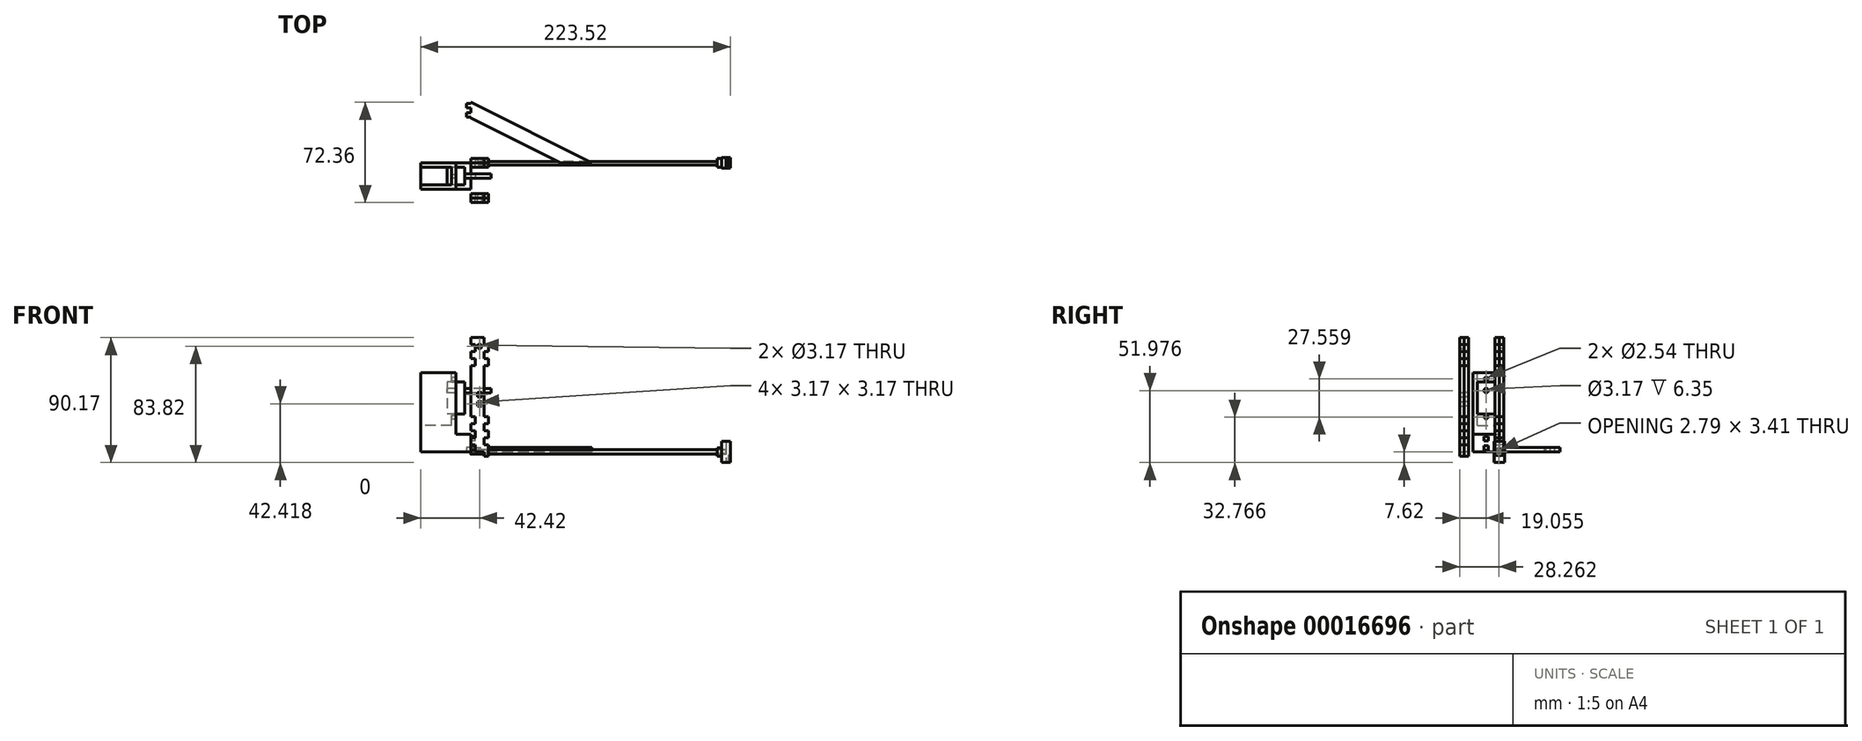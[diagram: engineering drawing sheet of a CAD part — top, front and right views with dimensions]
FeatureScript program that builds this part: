
annotation { "Feature Type Name" : "Feature", "Feature Type Description" : "" }
export const myFeature = defineFeature(function(context is Context, id is Id, definition is map)
    precondition{}
    {
        {
            var Q0;
            Q0=qCreatedBy(makeId("Right.planeOp"),FACE);
            var sketch = newSketch(context, id + "F0", { "sketchPlane" : qUnion([Q0])});
            skCircle(sketch, "E0.0", {"center": v(0, 0) * mm, "radius": 1.59 * mm});
            skPoint(sketch, "E1", {"position": v(0, 1.59) * mm});
            skSolve(sketch);
        }
        {
            var Q0;
            Q0=makeQuery(id+"F0.imprint","IMPRINT",FACE,{"disambiguationData":[TD([[makeQuery(id+"F0.imprint","IMPRINT",EDGE,{"derivedFrom":sQuery(id+"F0.wireOp",EDGE,"E0.0")}),1.0]])]});
            extrude(context, id + "F1", {"entities" : qUnion([Q0]), "depth" : 177.8 * mm});
        }
        {
            var Q0;
            Q0=qCreatedBy(makeId("Top.planeOp"),FACE);
            var Q1;
            Q1=sQuery(id+"F0.wireOp",VERTEX,"E1");
            cPlane(context, id + "F2", {"entities" : qUnion([Q0, Q1]), "cplaneType" : CPlaneType.PLANE_POINT, "offset" : 152.4 * mm, "width" : 152.4 * mm, "height" : 152.4 * mm});
        }
        {
            var Q0;
            Q0=qCreatedBy(id+"F2.planeOp",FACE);
            var sketch = newSketch(context, id + "F3", { "sketchPlane" : qUnion([Q0])});
            skLineSegment(sketch, "E2.0", {"start": v(0, 1.59) * mm, "end": v(0, -1.59) * mm});
            skLineSegment(sketch, "E3", {"start": v(0, 1.59) * mm, "end": v(177.8, 1.59) * mm, "construction": true});
            skLineSegment(sketch, "E4", {"start": v(177.8, -1.59) * mm, "end": v(0, -1.59) * mm, "construction": true});
            skLineSegment(sketch, "E5.bottom", {"start": v(27.11, 1.59) * mm, "end": v(88.9, 1.59) * mm});
            skLineSegment(sketch, "E5.top", {"start": v(27.11, 0.95) * mm, "end": v(88.9, 0.95) * mm});
            skLineSegment(sketch, "E5.left", {"start": v(27.11, 1.59) * mm, "end": v(27.11, 0.95) * mm});
            skLineSegment(sketch, "E5.right", {"start": v(88.9, 1.59) * mm, "end": v(88.9, 0.95) * mm});
            skLineSegment(sketch, "E6.0", {"start": v(177.8, 1.59) * mm, "end": v(177.8, -1.59) * mm});
            skLineSegment(sketch, "E7", {"start": v(88.9, 1.59) * mm, "end": v(88.9, -15.16) * mm, "construction": true});
            skLineSegment(sketch, "E8.0.MirrorCS", {"start": v(150.69, 0.95) * mm, "end": v(88.9, 0.95) * mm});
            skLineSegment(sketch, "E9.0.MirrorCS", {"start": v(150.69, 1.59) * mm, "end": v(88.9, 1.59) * mm});
            skLineSegment(sketch, "E10.0.MirrorCS", {"start": v(150.69, 1.59) * mm, "end": v(150.69, 0.95) * mm});
            skLineSegment(sketch, "E11.bottom", {"start": v(6.35, 1.59) * mm, "end": v(0, 1.59) * mm});
            skLineSegment(sketch, "E11.top", {"start": v(6.35, 0.95) * mm, "end": v(0, 0.95) * mm});
            skLineSegment(sketch, "E11.left", {"start": v(6.35, 1.59) * mm, "end": v(6.35, 0.95) * mm});
            skLineSegment(sketch, "E11.right", {"start": v(0, 1.59) * mm, "end": v(0, 0.95) * mm});
            skLineSegment(sketch, "E12.0.MirrorCS", {"start": v(171.45, 0.95) * mm, "end": v(177.8, 0.95) * mm});
            skLineSegment(sketch, "E13.0.MirrorCS", {"start": v(171.45, 1.59) * mm, "end": v(171.45, 0.95) * mm});
            skLineSegment(sketch, "E14.0.MirrorCS", {"start": v(177.8, 1.59) * mm, "end": v(177.8, 0.95) * mm});
            skLineSegment(sketch, "E15.0.MirrorCS", {"start": v(171.45, 1.59) * mm, "end": v(177.8, 1.59) * mm});
            skLineSegment(sketch, "E16.bottom", {"start": v(27.11, 1.59) * mm, "end": v(6.35, 1.59) * mm});
            skLineSegment(sketch, "E16.top", {"start": v(27.11, 0.95) * mm, "end": v(6.35, 0.95) * mm});
            skLineSegment(sketch, "E17.bottom", {"start": v(150.69, 1.59) * mm, "end": v(171.45, 1.59) * mm});
            skLineSegment(sketch, "E17.top", {"start": v(150.69, 0.95) * mm, "end": v(171.45, 0.95) * mm});
            skSolve(sketch);
        }
        {
            var Q0;
            {Q0=qUnion([makeQuery(id+"F3.imprint","IMPRINT",FACE,{"disambiguationData":[TD([[makeQuery(id+"F3.imprint","IMPRINT",EDGE,{"derivedFrom":sQuery(id+"F3.wireOp",EDGE,"E11.bottom")}),1.0]])]}),makeQuery(id+"F3.imprint","IMPRINT",FACE,{"disambiguationData":[TD([[makeQuery(id+"F3.imprint","IMPRINT",EDGE,{"derivedFrom":sQuery(id+"F3.wireOp",EDGE,"E12.0.MirrorCS")}),1.0]])]}),makeQuery(id+"F3.imprint","IMPRINT",FACE,{"disambiguationData":[TD([[makeQuery(id+"F3.imprint","IMPRINT",EDGE,{"derivedFrom":sQuery(id+"F3.wireOp",EDGE,"E5.bottom")}),-1.0]])]}),makeQuery(id+"F3.imprint","IMPRINT",FACE,{"disambiguationData":[TD([[makeQuery(id+"F3.imprint","IMPRINT",EDGE,{"derivedFrom":sQuery(id+"F3.wireOp",EDGE,"E8.0.MirrorCS")}),-1.0]])]}),makeQuery(id+"F3.imprint","IMPRINT",FACE,{"disambiguationData":[TD([[makeQuery(id+"F3.imprint","IMPRINT",EDGE,{"derivedFrom":sQuery(id+"F3.wireOp",EDGE,"E16.bottom")}),1.0]])]}),makeQuery(id+"F3.imprint","IMPRINT",FACE,{"disambiguationData":[TD([[makeQuery(id+"F3.imprint","IMPRINT",EDGE,{"derivedFrom":sQuery(id+"F3.wireOp",EDGE,"E17.bottom")}),-1.0]])]})]);}
            extrude(context, id + "F4", {"entities" : qUnion([Q0]), "operationType" : NewBodyOperationType.REMOVE, "endBound" : BoundingType.THROUGH_ALL, "oppositeDirection" : true, "depth" : 25.4 * mm});
        }
        {
            var Q0;
            Q0=qCreatedBy(makeId("Front.planeOp"),FACE);
            var sketch = newSketch(context, id + "F5", { "sketchPlane" : qUnion([Q0])});
            skLineSegment(sketch, "E18.bottom", {"start": v(0, 0) * mm, "end": v(12.7, 0) * mm});
            skLineSegment(sketch, "E18.top", {"start": v(0, 82.55) * mm, "end": v(12.7, 82.55) * mm});
            skLineSegment(sketch, "E18.left", {"start": v(0, 0) * mm, "end": v(0, 82.55) * mm});
            skLineSegment(sketch, "E18.right", {"start": v(12.7, 0) * mm, "end": v(12.7, 82.55) * mm});
            skLineSegment(sketch, "E19.bottom", {"start": v(12.7, 0) * mm, "end": v(9.53, 0) * mm});
            skLineSegment(sketch, "E19.top", {"start": v(12.7, -3.17) * mm, "end": v(9.53, -3.17) * mm});
            skLineSegment(sketch, "E19.left", {"start": v(12.7, 0) * mm, "end": v(12.7, -3.17) * mm});
            skLineSegment(sketch, "E19.right", {"start": v(9.53, 0) * mm, "end": v(9.53, -3.17) * mm});
            skLineSegment(sketch, "E20.bottom", {"start": v(12.7, 82.55) * mm, "end": v(9.52, 82.55) * mm});
            skLineSegment(sketch, "E20.top", {"start": v(12.7, 77.47) * mm, "end": v(9.52, 77.47) * mm});
            skLineSegment(sketch, "E20.left", {"start": v(12.7, 82.55) * mm, "end": v(12.7, 77.47) * mm});
            skLineSegment(sketch, "E20.right", {"start": v(9.52, 82.55) * mm, "end": v(9.52, 77.47) * mm});
            skLineSegment(sketch, "E21.bottom", {"start": v(9.52, 72.39) * mm, "end": v(12.7, 72.39) * mm});
            skLineSegment(sketch, "E21.top", {"start": v(9.52, 67.3) * mm, "end": v(12.7, 67.3) * mm});
            skLineSegment(sketch, "E21.left", {"start": v(9.52, 72.39) * mm, "end": v(9.52, 67.3) * mm});
            skLineSegment(sketch, "E21.right", {"start": v(12.7, 72.39) * mm, "end": v(12.7, 67.3) * mm});
            skLineSegment(sketch, "E22.bottom", {"start": v(9.52, 62.23) * mm, "end": v(12.7, 62.23) * mm});
            skLineSegment(sketch, "E22.top", {"start": v(9.53, 25.4) * mm, "end": v(12.7, 25.4) * mm});
            skLineSegment(sketch, "E22.left", {"start": v(9.52, 62.23) * mm, "end": v(9.52, 25.4) * mm});
            skLineSegment(sketch, "E22.right", {"start": v(12.7, 62.23) * mm, "end": v(12.7, 25.4) * mm});
            skLineSegment(sketch, "E23.bottom", {"start": v(9.53, 20.32) * mm, "end": v(12.7, 20.32) * mm});
            skLineSegment(sketch, "E23.top", {"start": v(9.53, 15.24) * mm, "end": v(12.7, 15.24) * mm});
            skLineSegment(sketch, "E23.left", {"start": v(9.52, 20.32) * mm, "end": v(9.52, 15.24) * mm});
            skLineSegment(sketch, "E23.right", {"start": v(12.7, 20.32) * mm, "end": v(12.7, 15.24) * mm});
            skLineSegment(sketch, "E24.bottom", {"start": v(9.53, 10.16) * mm, "end": v(12.7, 10.16) * mm});
            skLineSegment(sketch, "E24.top", {"start": v(9.53, 5.08) * mm, "end": v(12.7, 5.08) * mm});
            skLineSegment(sketch, "E24.left", {"start": v(9.52, 10.16) * mm, "end": v(9.52, 5.08) * mm});
            skLineSegment(sketch, "E24.right", {"start": v(12.7, 10.16) * mm, "end": v(12.7, 5.08) * mm});
            skLineSegment(sketch, "E25.bottom", {"start": v(0, 77.47) * mm, "end": v(3.18, 77.47) * mm});
            skLineSegment(sketch, "E25.top", {"start": v(0, 72.39) * mm, "end": v(3.18, 72.39) * mm});
            skLineSegment(sketch, "E25.left", {"start": v(0, 77.47) * mm, "end": v(0, 72.39) * mm});
            skLineSegment(sketch, "E25.right", {"start": v(3.18, 77.47) * mm, "end": v(3.18, 72.39) * mm});
            skLineSegment(sketch, "E26.bottom", {"start": v(0, 67.3) * mm, "end": v(3.18, 67.3) * mm});
            skLineSegment(sketch, "E26.top", {"start": v(0, 62.23) * mm, "end": v(3.18, 62.23) * mm});
            skLineSegment(sketch, "E26.left", {"start": v(0, 67.3) * mm, "end": v(0, 62.23) * mm});
            skLineSegment(sketch, "E26.right", {"start": v(3.18, 67.3) * mm, "end": v(3.18, 62.23) * mm});
            skLineSegment(sketch, "E27.bottom", {"start": v(0, 25.4) * mm, "end": v(3.18, 25.4) * mm});
            skLineSegment(sketch, "E27.top", {"start": v(0, 20.32) * mm, "end": v(3.18, 20.32) * mm});
            skLineSegment(sketch, "E27.left", {"start": v(0, 25.4) * mm, "end": v(0, 20.32) * mm});
            skLineSegment(sketch, "E27.right", {"start": v(3.18, 25.4) * mm, "end": v(3.18, 20.32) * mm});
            skLineSegment(sketch, "E28.bottom", {"start": v(0, 15.24) * mm, "end": v(3.18, 15.24) * mm});
            skLineSegment(sketch, "E28.top", {"start": v(0, 10.16) * mm, "end": v(3.18, 10.16) * mm});
            skLineSegment(sketch, "E28.left", {"start": v(0, 15.24) * mm, "end": v(0, 10.16) * mm});
            skLineSegment(sketch, "E28.right", {"start": v(3.18, 15.24) * mm, "end": v(3.18, 10.16) * mm});
            skLineSegment(sketch, "E29.bottom", {"start": v(0, 5.08) * mm, "end": v(3.18, 5.08) * mm});
            skLineSegment(sketch, "E29.top", {"start": v(0, 0) * mm, "end": v(3.18, 0) * mm});
            skLineSegment(sketch, "E29.left", {"start": v(0, 5.08) * mm, "end": v(0, 0) * mm});
            skLineSegment(sketch, "E29.right", {"start": v(3.18, 5.08) * mm, "end": v(3.18, 0) * mm});
            skPoint(sketch, "E30", {"position": v(6.35, 82.55) * mm});
            skPoint(sketch, "E31", {"position": v(6.35, 76.2) * mm});
            skSolve(sketch);
        }
        {
            var Q0;
            Q0=makeQuery(id+"F5.imprint","IMPRINT",FACE,{"disambiguationData":[TD([[makeQuery(id+"F5.imprint","IMPRINT",EDGE,{"derivedFrom":sQuery(id+"F5.wireOp",EDGE,"E18.bottom")}),1.0]])]});
            var Q1;
            Q1=makeQuery(id+"F5.imprint","IMPRINT",FACE,{"disambiguationData":[TD([[makeQuery(id+"F5.imprint","IMPRINT",EDGE,{"derivedFrom":sQuery(id+"F5.wireOp",EDGE,"E19.bottom")}),1.0]])]});
            extrude(context, id + "F6", {"entities" : qUnion([Q0, Q1]), "depth" : 3.17 * mm});
        }
        {
            var Q0;
            Q0=qCreatedBy(makeId("Front.planeOp"),FACE);
            var sketch = newSketch(context, id + "F7", { "sketchPlane" : qUnion([Q0])});
            skLineSegment(sketch, "E32.0.0", {"start": v(3.18, 5.08) * mm, "end": v(3.18, 0) * mm});
            skLineSegment(sketch, "E32.0.1", {"start": v(0, 5.08) * mm, "end": v(3.18, 5.08) * mm});
            skLineSegment(sketch, "E32.0.2", {"start": v(0, 5.08) * mm, "end": v(0, 10.16) * mm});
            skLineSegment(sketch, "E32.0.3", {"start": v(0, 10.16) * mm, "end": v(3.18, 10.16) * mm});
            skLineSegment(sketch, "E32.0.4", {"start": v(3.18, 15.24) * mm, "end": v(3.18, 10.16) * mm});
            skLineSegment(sketch, "E32.0.5", {"start": v(0, 15.24) * mm, "end": v(3.18, 15.24) * mm});
            skLineSegment(sketch, "E32.0.6", {"start": v(0, 15.24) * mm, "end": v(0, 20.32) * mm});
            skLineSegment(sketch, "E32.0.7", {"start": v(0, 20.32) * mm, "end": v(3.18, 20.32) * mm});
            skLineSegment(sketch, "E32.0.8", {"start": v(3.18, 25.4) * mm, "end": v(3.18, 20.32) * mm});
            skLineSegment(sketch, "E32.0.9", {"start": v(0, 25.4) * mm, "end": v(3.18, 25.4) * mm});
            skLineSegment(sketch, "E32.0.10", {"start": v(0, 25.4) * mm, "end": v(0, 62.23) * mm});
            skLineSegment(sketch, "E32.0.11", {"start": v(0, 62.23) * mm, "end": v(3.18, 62.23) * mm});
            skLineSegment(sketch, "E32.0.12", {"start": v(3.18, 67.3) * mm, "end": v(3.18, 62.23) * mm});
            skLineSegment(sketch, "E32.0.13", {"start": v(0, 67.3) * mm, "end": v(3.18, 67.3) * mm});
            skLineSegment(sketch, "E32.0.14", {"start": v(0, 67.3) * mm, "end": v(0, 72.39) * mm});
            skLineSegment(sketch, "E32.0.15", {"start": v(0, 72.39) * mm, "end": v(3.18, 72.39) * mm});
            skLineSegment(sketch, "E32.0.16", {"start": v(3.18, 77.47) * mm, "end": v(3.18, 72.39) * mm});
            skLineSegment(sketch, "E32.0.17", {"start": v(0, 77.47) * mm, "end": v(3.18, 77.47) * mm});
            skLineSegment(sketch, "E32.0.18", {"start": v(0, 77.47) * mm, "end": v(0, 82.55) * mm});
            skLineSegment(sketch, "E32.0.19", {"start": v(0, 82.55) * mm, "end": v(9.52, 82.55) * mm});
            skLineSegment(sketch, "E32.0.20", {"start": v(9.52, 82.55) * mm, "end": v(9.52, 77.47) * mm});
            skLineSegment(sketch, "E32.0.21", {"start": v(12.7, 77.47) * mm, "end": v(9.52, 77.47) * mm});
            skLineSegment(sketch, "E32.0.22", {"start": v(12.7, 72.39) * mm, "end": v(12.7, 77.47) * mm});
            skLineSegment(sketch, "E32.0.23", {"start": v(9.52, 72.39) * mm, "end": v(12.7, 72.39) * mm});
            skLineSegment(sketch, "E32.0.24", {"start": v(9.52, 72.39) * mm, "end": v(9.52, 67.3) * mm});
            skLineSegment(sketch, "E32.0.25", {"start": v(9.52, 67.3) * mm, "end": v(12.7, 67.3) * mm});
            skLineSegment(sketch, "E32.0.26", {"start": v(12.7, 62.23) * mm, "end": v(12.7, 67.3) * mm});
            skLineSegment(sketch, "E32.0.27", {"start": v(9.52, 62.23) * mm, "end": v(12.7, 62.23) * mm});
            skLineSegment(sketch, "E32.0.28", {"start": v(9.52, 62.23) * mm, "end": v(9.52, 25.4) * mm});
            skLineSegment(sketch, "E32.0.29", {"start": v(9.52, 25.4) * mm, "end": v(12.7, 25.4) * mm});
            skLineSegment(sketch, "E32.0.30", {"start": v(12.7, 20.32) * mm, "end": v(12.7, 25.4) * mm});
            skLineSegment(sketch, "E32.0.31", {"start": v(9.53, 20.32) * mm, "end": v(12.7, 20.32) * mm});
            skLineSegment(sketch, "E32.0.32", {"start": v(9.52, 20.32) * mm, "end": v(9.52, 15.24) * mm});
            skLineSegment(sketch, "E32.0.33", {"start": v(9.52, 15.24) * mm, "end": v(12.7, 15.24) * mm});
            skLineSegment(sketch, "E32.0.34", {"start": v(12.7, 10.16) * mm, "end": v(12.7, 15.24) * mm});
            skLineSegment(sketch, "E32.0.35", {"start": v(9.53, 10.16) * mm, "end": v(12.7, 10.16) * mm});
            skLineSegment(sketch, "E32.0.36", {"start": v(9.52, 10.16) * mm, "end": v(9.52, 5.08) * mm});
            skLineSegment(sketch, "E32.0.37", {"start": v(9.52, 5.08) * mm, "end": v(12.7, 5.08) * mm});
            skLineSegment(sketch, "E32.0.38", {"start": v(12.7, -3.17) * mm, "end": v(12.7, 5.08) * mm});
            skLineSegment(sketch, "E32.0.39", {"start": v(12.7, -3.17) * mm, "end": v(9.53, -3.17) * mm});
            skLineSegment(sketch, "E32.0.40", {"start": v(9.53, 0) * mm, "end": v(9.53, -3.17) * mm});
            skLineSegment(sketch, "E32.0.41", {"start": v(3.18, 0) * mm, "end": v(9.53, 0) * mm});
            skLineSegment(sketch, "E33", {"start": v(6.35, 82.55) * mm, "end": v(6.35, 0) * mm, "construction": true});
            skCircle(sketch, "E34", {"center": v(6.35, 76.2) * mm, "radius": 1.59 * mm});
            skSolve(sketch);
        }
        {
            var Q0;
            Q0=makeQuery(id+"F7.imprint","IMPRINT",FACE,{"disambiguationData":[TD([[makeQuery(id+"F7.imprint","IMPRINT",EDGE,{"derivedFrom":sQuery(id+"F7.wireOp",EDGE,"E32.0.0")}),1.0]])]});
            extrude(context, id + "F8", {"entities" : qUnion([Q0]), "oppositeDirection" : true, "depth" : 3.17 * mm});
        }
        {
            var Q0;
            Q0=qCreatedBy(makeId("Front.planeOp"),FACE);
            cPlane(context, id + "F9", {"entities" : qUnion([Q0]), "cplaneType" : CPlaneType.OFFSET, "offset" : 25.4 * mm, "width" : 152.4 * mm, "height" : 152.4 * mm});
        }
        {
            var Q0;
            Q0=qCreatedBy(id+"F9.planeOp",FACE);
            var sketch = newSketch(context, id + "F10", { "sketchPlane" : qUnion([Q0])});
            skLineSegment(sketch, "E35.0.0", {"start": v(0, 5.08) * mm, "end": v(3.18, 5.08) * mm});
            skLineSegment(sketch, "E35.0.1", {"start": v(0, 5.08) * mm, "end": v(0, 10.16) * mm});
            skLineSegment(sketch, "E35.0.2", {"start": v(0, 10.16) * mm, "end": v(3.18, 10.16) * mm});
            skLineSegment(sketch, "E35.0.3", {"start": v(3.18, 15.24) * mm, "end": v(3.18, 10.16) * mm});
            skLineSegment(sketch, "E35.0.4", {"start": v(0, 15.24) * mm, "end": v(3.18, 15.24) * mm});
            skLineSegment(sketch, "E35.0.5", {"start": v(0, 15.24) * mm, "end": v(0, 20.32) * mm});
            skLineSegment(sketch, "E35.0.6", {"start": v(0, 20.32) * mm, "end": v(3.18, 20.32) * mm});
            skLineSegment(sketch, "E35.0.7", {"start": v(3.18, 25.4) * mm, "end": v(3.18, 20.32) * mm});
            skLineSegment(sketch, "E35.0.8", {"start": v(0, 25.4) * mm, "end": v(3.18, 25.4) * mm});
            skLineSegment(sketch, "E35.0.9", {"start": v(0, 25.4) * mm, "end": v(0, 62.23) * mm});
            skLineSegment(sketch, "E35.0.10", {"start": v(0, 62.23) * mm, "end": v(3.18, 62.23) * mm});
            skLineSegment(sketch, "E35.0.11", {"start": v(3.18, 67.3) * mm, "end": v(3.18, 62.23) * mm});
            skLineSegment(sketch, "E35.0.12", {"start": v(0, 67.3) * mm, "end": v(3.18, 67.3) * mm});
            skLineSegment(sketch, "E35.0.13", {"start": v(0, 67.3) * mm, "end": v(0, 72.39) * mm});
            skLineSegment(sketch, "E35.0.14", {"start": v(0, 72.39) * mm, "end": v(3.18, 72.39) * mm});
            skLineSegment(sketch, "E35.0.15", {"start": v(3.18, 77.47) * mm, "end": v(3.18, 72.39) * mm});
            skLineSegment(sketch, "E35.0.16", {"start": v(0, 77.47) * mm, "end": v(3.18, 77.47) * mm});
            skLineSegment(sketch, "E35.0.17", {"start": v(0, 77.47) * mm, "end": v(0, 82.55) * mm});
            skLineSegment(sketch, "E35.0.18", {"start": v(0, 82.55) * mm, "end": v(9.52, 82.55) * mm});
            skLineSegment(sketch, "E35.0.19", {"start": v(9.52, 82.55) * mm, "end": v(9.52, 77.47) * mm});
            skLineSegment(sketch, "E35.0.20", {"start": v(12.7, 77.47) * mm, "end": v(9.52, 77.47) * mm});
            skLineSegment(sketch, "E35.0.21", {"start": v(12.7, 72.39) * mm, "end": v(12.7, 77.47) * mm});
            skLineSegment(sketch, "E35.0.22", {"start": v(9.52, 72.39) * mm, "end": v(12.7, 72.39) * mm});
            skLineSegment(sketch, "E35.0.23", {"start": v(9.52, 72.39) * mm, "end": v(9.52, 67.3) * mm});
            skLineSegment(sketch, "E35.0.24", {"start": v(9.52, 67.3) * mm, "end": v(12.7, 67.3) * mm});
            skLineSegment(sketch, "E35.0.25", {"start": v(12.7, 62.23) * mm, "end": v(12.7, 67.3) * mm});
            skLineSegment(sketch, "E35.0.26", {"start": v(9.52, 62.23) * mm, "end": v(12.7, 62.23) * mm});
            skLineSegment(sketch, "E35.0.27", {"start": v(9.52, 62.23) * mm, "end": v(9.52, 25.4) * mm});
            skLineSegment(sketch, "E35.0.28", {"start": v(9.52, 25.4) * mm, "end": v(12.7, 25.4) * mm});
            skLineSegment(sketch, "E35.0.29", {"start": v(12.7, 20.32) * mm, "end": v(12.7, 25.4) * mm});
            skLineSegment(sketch, "E35.0.30", {"start": v(9.53, 20.32) * mm, "end": v(12.7, 20.32) * mm});
            skLineSegment(sketch, "E35.0.31", {"start": v(9.52, 20.32) * mm, "end": v(9.52, 15.24) * mm});
            skLineSegment(sketch, "E35.0.32", {"start": v(9.52, 15.24) * mm, "end": v(12.7, 15.24) * mm});
            skLineSegment(sketch, "E35.0.33", {"start": v(12.7, 10.16) * mm, "end": v(12.7, 15.24) * mm});
            skLineSegment(sketch, "E35.0.34", {"start": v(9.53, 10.16) * mm, "end": v(12.7, 10.16) * mm});
            skLineSegment(sketch, "E35.0.35", {"start": v(9.52, 10.16) * mm, "end": v(9.52, 5.08) * mm});
            skLineSegment(sketch, "E35.0.36", {"start": v(9.52, 5.08) * mm, "end": v(12.7, 5.08) * mm});
            skLineSegment(sketch, "E35.0.37", {"start": v(12.7, -3.17) * mm, "end": v(12.7, 5.08) * mm});
            skLineSegment(sketch, "E35.0.38", {"start": v(12.7, -3.17) * mm, "end": v(9.53, -3.17) * mm});
            skLineSegment(sketch, "E35.0.39", {"start": v(9.53, 0) * mm, "end": v(9.53, -3.17) * mm});
            skLineSegment(sketch, "E35.0.40", {"start": v(3.18, 0) * mm, "end": v(9.53, 0) * mm});
            skLineSegment(sketch, "E35.0.41", {"start": v(3.18, 5.08) * mm, "end": v(3.18, 0) * mm});
            skLineSegment(sketch, "E36.0", {"start": v(6.35, 82.55) * mm, "end": v(6.35, 0) * mm, "construction": true});
            skLineSegment(sketch, "E37.rect.bottom", {"start": v(4.76, 39.81) * mm, "end": v(7.94, 39.81) * mm});
            skLineSegment(sketch, "E37.rect.top", {"start": v(4.76, 42.99) * mm, "end": v(7.94, 42.99) * mm});
            skLineSegment(sketch, "E37.rect.left", {"start": v(4.76, 39.81) * mm, "end": v(4.76, 42.99) * mm});
            skLineSegment(sketch, "E37.rect.right", {"start": v(7.94, 39.81) * mm, "end": v(7.94, 42.99) * mm});
            skPoint(sketch, "E37.rect.middle", {"position": v(6.35, 41.4) * mm});
            skLineSegment(sketch, "E38.rect.bottom", {"start": v(4.76, 33.21) * mm, "end": v(7.94, 33.21) * mm});
            skLineSegment(sketch, "E38.rect.top", {"start": v(4.76, 36.39) * mm, "end": v(7.94, 36.39) * mm});
            skLineSegment(sketch, "E38.rect.left", {"start": v(4.76, 33.21) * mm, "end": v(4.76, 36.39) * mm});
            skLineSegment(sketch, "E38.rect.right", {"start": v(7.94, 33.21) * mm, "end": v(7.94, 36.39) * mm});
            skPoint(sketch, "E38.rect.middle", {"position": v(6.35, 34.8) * mm});
            skPoint(sketch, "E39", {"position": v(6.35, 38.1) * mm});
            skCircle(sketch, "E40.0", {"center": v(6.35, 76.2) * mm, "radius": 1.59 * mm});
            skSolve(sketch);
        }
        {
            var Q0;
            Q0=makeQuery(id+"F10.imprint","IMPRINT",FACE,{"disambiguationData":[TD([[makeQuery(id+"F10.imprint","IMPRINT",EDGE,{"derivedFrom":sQuery(id+"F10.wireOp",EDGE,"E35.0.0")}),1.0]])]});
            extrude(context, id + "F11", {"entities" : qUnion([Q0]), "depth" : 3.17 * mm});
        }
        {
            var Q0;
            Q0=qCreatedBy(id+"F9.planeOp",FACE);
            var sketch = newSketch(context, id + "F12", { "sketchPlane" : qUnion([Q0])});
            skLineSegment(sketch, "E41.0.0", {"start": v(0, 5.08) * mm, "end": v(0, 10.16) * mm});
            skLineSegment(sketch, "E41.0.1", {"start": v(0, 10.16) * mm, "end": v(3.18, 10.16) * mm});
            skLineSegment(sketch, "E41.0.2", {"start": v(3.18, 15.24) * mm, "end": v(3.18, 10.16) * mm});
            skLineSegment(sketch, "E41.0.3", {"start": v(0, 15.24) * mm, "end": v(3.18, 15.24) * mm});
            skLineSegment(sketch, "E41.0.4", {"start": v(0, 15.24) * mm, "end": v(0, 20.32) * mm});
            skLineSegment(sketch, "E41.0.5", {"start": v(0, 20.32) * mm, "end": v(3.18, 20.32) * mm});
            skLineSegment(sketch, "E41.0.6", {"start": v(3.18, 25.4) * mm, "end": v(3.18, 20.32) * mm});
            skLineSegment(sketch, "E41.0.7", {"start": v(0, 25.4) * mm, "end": v(3.18, 25.4) * mm});
            skLineSegment(sketch, "E41.0.8", {"start": v(0, 25.4) * mm, "end": v(0, 62.23) * mm});
            skLineSegment(sketch, "E41.0.9", {"start": v(0, 62.23) * mm, "end": v(3.18, 62.23) * mm});
            skLineSegment(sketch, "E41.0.10", {"start": v(3.18, 67.3) * mm, "end": v(3.18, 62.23) * mm});
            skLineSegment(sketch, "E41.0.11", {"start": v(0, 67.3) * mm, "end": v(3.18, 67.3) * mm});
            skLineSegment(sketch, "E41.0.12", {"start": v(0, 67.3) * mm, "end": v(0, 72.39) * mm});
            skLineSegment(sketch, "E41.0.13", {"start": v(0, 72.39) * mm, "end": v(3.18, 72.39) * mm});
            skLineSegment(sketch, "E41.0.14", {"start": v(3.18, 77.47) * mm, "end": v(3.18, 72.39) * mm});
            skLineSegment(sketch, "E41.0.15", {"start": v(0, 77.47) * mm, "end": v(3.18, 77.47) * mm});
            skLineSegment(sketch, "E41.0.16", {"start": v(0, 77.47) * mm, "end": v(0, 82.55) * mm});
            skLineSegment(sketch, "E41.0.17", {"start": v(0, 82.55) * mm, "end": v(9.52, 82.55) * mm});
            skLineSegment(sketch, "E41.0.18", {"start": v(9.52, 82.55) * mm, "end": v(9.52, 77.47) * mm});
            skLineSegment(sketch, "E41.0.19", {"start": v(12.7, 77.47) * mm, "end": v(9.52, 77.47) * mm});
            skLineSegment(sketch, "E41.0.20", {"start": v(12.7, 72.39) * mm, "end": v(12.7, 77.47) * mm});
            skLineSegment(sketch, "E41.0.21", {"start": v(9.52, 72.39) * mm, "end": v(12.7, 72.39) * mm});
            skLineSegment(sketch, "E41.0.22", {"start": v(9.52, 72.39) * mm, "end": v(9.52, 67.3) * mm});
            skLineSegment(sketch, "E41.0.23", {"start": v(9.52, 67.3) * mm, "end": v(12.7, 67.3) * mm});
            skLineSegment(sketch, "E41.0.24", {"start": v(12.7, 62.23) * mm, "end": v(12.7, 67.3) * mm});
            skLineSegment(sketch, "E41.0.25", {"start": v(9.52, 62.23) * mm, "end": v(12.7, 62.23) * mm});
            skLineSegment(sketch, "E41.0.26", {"start": v(9.52, 62.23) * mm, "end": v(9.52, 25.4) * mm});
            skLineSegment(sketch, "E41.0.27", {"start": v(9.52, 25.4) * mm, "end": v(12.7, 25.4) * mm});
            skLineSegment(sketch, "E41.0.28", {"start": v(12.7, 20.32) * mm, "end": v(12.7, 25.4) * mm});
            skLineSegment(sketch, "E41.0.29", {"start": v(9.53, 20.32) * mm, "end": v(12.7, 20.32) * mm});
            skLineSegment(sketch, "E41.0.30", {"start": v(9.52, 20.32) * mm, "end": v(9.52, 15.24) * mm});
            skLineSegment(sketch, "E41.0.31", {"start": v(9.52, 15.24) * mm, "end": v(12.7, 15.24) * mm});
            skLineSegment(sketch, "E41.0.32", {"start": v(12.7, 10.16) * mm, "end": v(12.7, 15.24) * mm});
            skLineSegment(sketch, "E41.0.33", {"start": v(9.53, 10.16) * mm, "end": v(12.7, 10.16) * mm});
            skLineSegment(sketch, "E41.0.34", {"start": v(9.52, 10.16) * mm, "end": v(9.52, 5.08) * mm});
            skLineSegment(sketch, "E41.0.35", {"start": v(9.52, 5.08) * mm, "end": v(12.7, 5.08) * mm});
            skLineSegment(sketch, "E41.0.36", {"start": v(12.7, -3.17) * mm, "end": v(12.7, 5.08) * mm});
            skLineSegment(sketch, "E41.0.37", {"start": v(12.7, -3.17) * mm, "end": v(9.53, -3.17) * mm});
            skLineSegment(sketch, "E41.0.38", {"start": v(9.53, 0) * mm, "end": v(9.53, -3.17) * mm});
            skLineSegment(sketch, "E41.0.39", {"start": v(3.18, 0) * mm, "end": v(9.53, 0) * mm});
            skLineSegment(sketch, "E41.0.40", {"start": v(3.18, 5.08) * mm, "end": v(3.18, 0) * mm});
            skLineSegment(sketch, "E41.0.41", {"start": v(0, 5.08) * mm, "end": v(3.18, 5.08) * mm});
            skLineSegment(sketch, "E42.0", {"start": v(4.76, 39.81) * mm, "end": v(7.94, 39.81) * mm});
            skLineSegment(sketch, "E43.0", {"start": v(7.94, 39.81) * mm, "end": v(7.94, 42.99) * mm});
            skLineSegment(sketch, "E44.0", {"start": v(4.76, 42.99) * mm, "end": v(7.94, 42.99) * mm});
            skLineSegment(sketch, "E45.0", {"start": v(4.76, 39.81) * mm, "end": v(4.76, 42.99) * mm});
            skLineSegment(sketch, "E46.0", {"start": v(4.76, 36.39) * mm, "end": v(7.94, 36.39) * mm});
            skLineSegment(sketch, "E47.0", {"start": v(7.94, 33.21) * mm, "end": v(7.94, 36.39) * mm});
            skLineSegment(sketch, "E48.0", {"start": v(4.76, 33.21) * mm, "end": v(7.94, 33.21) * mm});
            skLineSegment(sketch, "E49.0", {"start": v(4.76, 33.21) * mm, "end": v(4.76, 36.39) * mm});
            skSolve(sketch);
        }
        {
            var Q0;
            Q0=makeQuery(id+"F12.imprint","IMPRINT",FACE,{"disambiguationData":[TD([[makeQuery(id+"F12.imprint","IMPRINT",EDGE,{"derivedFrom":sQuery(id+"F12.wireOp",EDGE,"E41.0.0")}),-1.0]])]});
            extrude(context, id + "F13", {"entities" : qUnion([Q0]), "oppositeDirection" : true, "depth" : 3.17 * mm});
        }
        {
            var Q0;
            Q0=qCreatedBy(makeId("Top.planeOp"),FACE);
            var sketch = newSketch(context, id + "F14", { "sketchPlane" : qUnion([Q0])});
            skPoint(sketch, "E50", {"position": v(76.2, 0) * mm});
            skPoint(sketch, "E51", {"position": v(0, 38.1) * mm});
            skLineSegment(sketch, "E52", {"start": v(0, 32.42) * mm, "end": v(64.84, 0) * mm});
            skLineSegment(sketch, "E53", {"start": v(87.56, 0) * mm, "end": v(0, 43.78) * mm});
            skLineSegment(sketch, "E54", {"start": v(0, 43.78) * mm, "end": v(0, 32.42) * mm});
            skPoint(sketch, "E55.orphan", {"position": v(2.27, 42.64) * mm});
            skPoint(sketch, "E56.orphan", {"position": v(-2.27, 33.56) * mm});
            skLineSegment(sketch, "E57", {"start": v(64.84, 0) * mm, "end": v(87.56, 0) * mm});
            skPoint(sketch, "E58.orphan", {"position": v(73.93, -4.54) * mm});
            skPoint(sketch, "E59.end.orphan", {"position": v(78.47, 4.54) * mm});
            skLineSegment(sketch, "E60.bottom", {"start": v(0, 39.81) * mm, "end": v(-3.17, 39.81) * mm});
            skLineSegment(sketch, "E60.top", {"start": v(0, 42.99) * mm, "end": v(-3.17, 42.99) * mm});
            skLineSegment(sketch, "E60.right", {"start": v(-3.17, 39.81) * mm, "end": v(-3.17, 42.99) * mm});
            skLineSegment(sketch, "E61.bottom", {"start": v(0, 33.21) * mm, "end": v(-3.17, 33.21) * mm});
            skLineSegment(sketch, "E61.top", {"start": v(0, 36.39) * mm, "end": v(-3.17, 36.39) * mm});
            skLineSegment(sketch, "E61.right", {"start": v(-3.17, 33.21) * mm, "end": v(-3.17, 36.39) * mm});
            skLineSegment(sketch, "E62.bottom", {"start": v(77.91, 0) * mm, "end": v(81.09, 0) * mm});
            skLineSegment(sketch, "E62.top", {"start": v(77.91, -3.17) * mm, "end": v(81.09, -3.17) * mm});
            skLineSegment(sketch, "E62.left", {"start": v(77.91, 0) * mm, "end": v(77.91, -3.17) * mm});
            skLineSegment(sketch, "E62.right", {"start": v(81.09, 0) * mm, "end": v(81.09, -3.17) * mm});
            skLineSegment(sketch, "E63.bottom", {"start": v(71.31, 0) * mm, "end": v(74.49, 0) * mm});
            skLineSegment(sketch, "E63.top", {"start": v(71.31, -3.17) * mm, "end": v(74.49, -3.17) * mm});
            skLineSegment(sketch, "E63.left", {"start": v(71.31, 0) * mm, "end": v(71.31, -3.17) * mm});
            skLineSegment(sketch, "E63.right", {"start": v(74.49, 0) * mm, "end": v(74.49, -3.17) * mm});
            skSolve(sketch);
        }
        {
            var Q0;
            {var subQ1=sQuery(id+"F14.wireOp",EDGE,"E60.bottom");var subQ7=sQuery(id+"F14.wireOp",EDGE,"E61.bottom");var subQ13=sQuery(id+"F14.wireOp",EDGE,"E62.bottom");var subQ14=makeQuery(id+"F14.imprint","IMPRINT",EDGE,{"derivedFrom":subQ13});var subQ17=sQuery(id+"F14.wireOp",EDGE,"E63.bottom");var subQ18=makeQuery(id+"F14.imprint","IMPRINT",EDGE,{"derivedFrom":subQ17});var subQ21=sQuery(id+"F14.wireOp",EDGE,"E52");Q0=qUnion([makeQuery(id+"F14.imprint","IMPRINT",FACE,{"disambiguationData":[TD([[makeQuery(id+"F14.imprint","IMPRINT",EDGE,{"derivedFrom":subQ1}),-1.0]])]}),makeQuery(id+"F14.imprint","IMPRINT",FACE,{"disambiguationData":[TD([[makeQuery(id+"F14.imprint","IMPRINT",EDGE,{"derivedFrom":subQ7}),-1.0]])]}),makeQuery(id+"F14.imprint","IMPRINT",FACE,{"disambiguationData":[TD([[subQ14,-1.0]])]}),makeQuery(id+"F14.imprint","IMPRINT",FACE,{"disambiguationData":[TD([[subQ18,-1.0]])]}),makeQuery(id+"F14.imprint","IMPRINT",FACE,{"disambiguationData":[TD([[makeQuery(id+"F14.imprint","IMPRINT",EDGE,{"derivedFrom":subQ21}),1.0]])]})]);}
            extrude(context, id + "F15", {"entities" : qUnion([Q0]), "depth" : 3.17 * mm});
        }
        {
            var Q0;
            Q0=makeQuery(id+"F1.opExtrude","CAP_FACE",FACE,{"disambiguationData":[OSD([sQuery(id+"F0.wireOp",EDGE,"E0.0")])],"isStart":false});
            var sketch = newSketch(context, id + "F16", { "sketchPlane" : qUnion([Q0])});
            skLineSegment(sketch, "E64.0.0", {"start": v(0.95, -1.27) * mm, "end": v(0.95, 1.27) * mm});
            skArc(sketch, "E64.0.1", {"start": v(0.95, 1.27) * mm, "mid": v(-1.59, 0) * mm, "end": v(0.95, -1.27) * mm});
            skCircle(sketch, "E65", {"center": v(0, 0) * mm, "radius": 3.08 * mm});
            skLineSegment(sketch, "E66.0", {"start": v(1.08, -1.33) * mm, "end": v(1.08, 1.33) * mm});
            skArc(sketch, "E66.1", {"start": v(1.08, 1.33) * mm, "mid": v(-1.71, 0) * mm, "end": v(1.08, -1.33) * mm});
            skSolve(sketch);
        }
        {
            var Q0;
            Q0=makeQuery(id+"F16.imprint","IMPRINT",FACE,{"disambiguationData":[TD([[makeQuery(id+"F16.imprint","IMPRINT",EDGE,{"derivedFrom":sQuery(id+"F16.wireOp",EDGE,"E65")}),1.0]])]});
            extrude(context, id + "F17", {"entities" : qUnion([Q0]), "depth" : 6.35 * mm});
        }
        {
            var Q0;
            Q0=makeQuery(id+"F17.opExtrude","CAP_FACE",FACE,{"disambiguationData":[OSD([sQuery(id+"F16.wireOp",EDGE,"E65"),sQuery(id+"F16.wireOp",EDGE,"E66.0"),sQuery(id+"F16.wireOp",EDGE,"E66.1")])],"isStart":false});
            var sketch = newSketch(context, id + "F18", { "sketchPlane" : qUnion([Q0])});
            skLineSegment(sketch, "E67.rect.bottom", {"start": v(3.8, -7.62) * mm, "end": v(-3.81, -7.62) * mm});
            skLineSegment(sketch, "E67.rect.top", {"start": v(3.8, 7.62) * mm, "end": v(-3.81, 7.62) * mm});
            skLineSegment(sketch, "E67.rect.left", {"start": v(3.81, -7.62) * mm, "end": v(3.81, 7.62) * mm});
            skLineSegment(sketch, "E67.rect.right", {"start": v(-3.81, -7.62) * mm, "end": v(-3.8, 7.62) * mm});
            skPoint(sketch, "E67.rect.middle", {"position": v(0, 0) * mm});
            skSolve(sketch);
        }
        {
            var Q0;
            Q0=makeQuery(id+"F18.imprint","IMPRINT",FACE,{"disambiguationData":[TD([[makeQuery(id+"F18.imprint","IMPRINT",EDGE,{"derivedFrom":sQuery(id+"F18.wireOp",EDGE,"E67.rect.bottom")}),-1.0]])]});
            var Q1;
            Q1=makeQuery(id+"F18.imprint","IMPRINT",FACE,{"disambiguationData":[TD([[makeQuery(id+"F18.imprint","IMPRINT",EDGE,{"derivedFrom":makeQuery(id+"F17.opExtrude","CAP_EDGE",EDGE,{"disambiguationData":[OSD([sQuery(id+"F16.wireOp",EDGE,"E65")])],"isStart":false})}),1.0]])]});
            extrude(context, id + "F19", {"entities" : qUnion([Q0, Q1]), "operationType" : NewBodyOperationType.ADD, "oppositeDirection" : true, "depth" : 3.17 * mm});
        }
        {
            var Q0;
            {var subQ0=sQuery(id+"F16.wireOp",EDGE,"E66.0");var subQ1=sQuery(id+"F16.wireOp",EDGE,"E66.1");Q0=makeQuery(id+"F19.boolean.opBoolean","MERGE",FACE,{"derivedFrom":[makeQuery(id+"F17.opExtrude","CAP_FACE",FACE,{"disambiguationData":[OSD([sQuery(id+"F16.wireOp",EDGE,"E65"),subQ0,subQ1])],"isStart":false}),makeQuery(id+"F19.opExtrude","CAP_FACE",FACE,{"disambiguationData":[OSD([subQ0,subQ1,sQuery(id+"F18.wireOp",EDGE,"E67.rect.bottom"),sQuery(id+"F18.wireOp",EDGE,"E67.rect.top"),sQuery(id+"F18.wireOp",EDGE,"E67.rect.left"),sQuery(id+"F18.wireOp",EDGE,"E67.rect.right")])],"isStart":true})]});}
            var sketch = newSketch(context, id + "F20", { "sketchPlane" : qUnion([Q0])});
            skLineSegment(sketch, "E68.bottom", {"start": v(-3.09, 7.62) * mm, "end": v(3.09, 7.62) * mm});
            skLineSegment(sketch, "E68.top", {"start": v(-3.09, -7.62) * mm, "end": v(3.09, -7.62) * mm});
            skLineSegment(sketch, "E68.left", {"start": v(-3.09, 7.62) * mm, "end": v(-3.09, -7.62) * mm});
            skLineSegment(sketch, "E68.right", {"start": v(3.09, 7.62) * mm, "end": v(3.09, -7.62) * mm});
            skPoint(sketch, "E69", {"position": v(0, 7.62) * mm});
            skLineSegment(sketch, "E70", {"start": v(-3.09, -2.54) * mm, "end": v(3.09, -2.54) * mm});
            skSolve(sketch);
        }
        {
            var Q0;
            {var subQ3=makeQuery(id+"F19.opExtrude","CAP_EDGE",EDGE,{"disambiguationData":[OSD([sQuery(id+"F18.wireOp",EDGE,"E67.rect.right")])],"isStart":true});Q0=makeQuery(id+"F20.imprint","IMPRINT",FACE,{"disambiguationData":[TD([[makeQuery(id+"F20.imprint","IMPRINT",EDGE,{"derivedFrom":subQ3}),-1.0]])]});}
            var Q1;
            {var subQ3=sQuery(id+"F20.wireOp",EDGE,"E68.top");Q1=makeQuery(id+"F20.imprint","IMPRINT",FACE,{"disambiguationData":[TD([[makeQuery(id+"F20.imprint","IMPRINT",EDGE,{"derivedFrom":subQ3}),-1.0]])]});}
            var Q2;
            {var subQ3=makeQuery(id+"F19.opExtrude","CAP_EDGE",EDGE,{"disambiguationData":[OSD([sQuery(id+"F18.wireOp",EDGE,"E67.rect.left")])],"isStart":true});Q2=makeQuery(id+"F20.imprint","IMPRINT",FACE,{"disambiguationData":[TD([[makeQuery(id+"F20.imprint","IMPRINT",EDGE,{"derivedFrom":subQ3}),1.0]])]});}
            extrude(context, id + "F21", {"entities" : qUnion([Q0, Q1, Q2]), "operationType" : NewBodyOperationType.ADD, "depth" : 3.3 * mm});
        }
        {
            var Q0;
            {var subQ3=sQuery(id+"F20.wireOp",EDGE,"E68.top");Q0=makeQuery(id+"F20.imprint","IMPRINT",FACE,{"disambiguationData":[TD([[makeQuery(id+"F20.imprint","IMPRINT",EDGE,{"derivedFrom":subQ3}),-1.0]])]});}
            extrude(context, id + "F22", {"entities" : qUnion([Q0]), "operationType" : NewBodyOperationType.REMOVE, "depth" : 1.65 * mm});
        }
        {
            var Q0;
            Q0=qCreatedBy(makeId("Front.planeOp"),FACE);
            var sketch = newSketch(context, id + "F23", { "sketchPlane" : qUnion([Q0])});
            skLineSegment(sketch, "E71.bottom", {"start": v(0, 0) * mm, "end": v(-36.07, 0) * mm});
            skLineSegment(sketch, "E71.top", {"start": v(-10.67, 57.15) * mm, "end": v(-36.07, 57.15) * mm});
            skLineSegment(sketch, "E71.left", {"start": v(0, 0) * mm, "end": v(0, 12.7) * mm});
            skLineSegment(sketch, "E71.right", {"start": v(-36.07, 0) * mm, "end": v(-36.07, 57.15) * mm});
            skLineSegment(sketch, "E72.top", {"start": v(-10.67, 12.7) * mm, "end": v(0, 12.7) * mm});
            skLineSegment(sketch, "E72.left", {"start": v(-10.67, 57.15) * mm, "end": v(-10.67, 12.7) * mm});
            skPoint(sketch, "E73", {"position": v(0, 6.35) * mm});
            skPoint(sketch, "E74", {"position": v(-10.67, 44.45) * mm});
            skSolve(sketch);
        }
        {
            var Q0;
            Q0=makeQuery(id+"F23.imprint","IMPRINT",FACE,{"disambiguationData":[TD([[makeQuery(id+"F23.imprint","IMPRINT",EDGE,{"derivedFrom":sQuery(id+"F23.wireOp",EDGE,"E71.bottom")}),-1.0]])]});
            extrude(context, id + "F24", {"entities" : qUnion([Q0]), "depth" : 19.05 * mm});
        }
        {
            var Q0;
            Q0=makeQuery(id+"F24.opExtrude","SWEPT_FACE",FACE,{"disambiguationData":[OSD([sQuery(id+"F23.wireOp",EDGE,"E71.left")])]});
            var sketch = newSketch(context, id + "F25", { "sketchPlane" : qUnion([Q0])});
            skLineSegment(sketch, "E75", {"start": v(-9.53, 12.7) * mm, "end": v(-9.53, 0) * mm, "construction": true});
            skLineSegment(sketch, "E76", {"start": v(-19.05, 6.35) * mm, "end": v(0, 6.35) * mm, "construction": true});
            skLineSegment(sketch, "E77.rect.bottom", {"start": v(-7.94, 8.06) * mm, "end": v(-11.11, 8.06) * mm});
            skLineSegment(sketch, "E77.rect.top", {"start": v(-7.94, 11.24) * mm, "end": v(-11.11, 11.24) * mm});
            skLineSegment(sketch, "E77.rect.left", {"start": v(-7.94, 8.06) * mm, "end": v(-7.94, 11.24) * mm});
            skLineSegment(sketch, "E77.rect.right", {"start": v(-11.11, 8.06) * mm, "end": v(-11.11, 11.24) * mm});
            skPoint(sketch, "E77.rect.middle", {"position": v(-9.53, 9.65) * mm});
            skLineSegment(sketch, "E78.rect.bottom", {"start": v(-7.94, 1.46) * mm, "end": v(-11.11, 1.46) * mm});
            skLineSegment(sketch, "E78.rect.top", {"start": v(-7.94, 4.64) * mm, "end": v(-11.11, 4.64) * mm});
            skLineSegment(sketch, "E78.rect.left", {"start": v(-7.94, 1.46) * mm, "end": v(-7.94, 4.64) * mm});
            skLineSegment(sketch, "E78.rect.right", {"start": v(-11.11, 1.46) * mm, "end": v(-11.11, 4.64) * mm});
            skPoint(sketch, "E78.rect.middle", {"position": v(-9.53, 3.05) * mm});
            skSolve(sketch);
        }
        {
            var Q0;
            Q0=makeQuery(id+"F25.imprint","IMPRINT",FACE,{"disambiguationData":[TD([[makeQuery(id+"F25.imprint","IMPRINT",EDGE,{"derivedFrom":sQuery(id+"F25.wireOp",EDGE,"E77.rect.bottom")}),-1.0]])]});
            var Q1;
            Q1=makeQuery(id+"F25.imprint","IMPRINT",FACE,{"disambiguationData":[TD([[makeQuery(id+"F25.imprint","IMPRINT",EDGE,{"derivedFrom":sQuery(id+"F25.wireOp",EDGE,"E78.rect.bottom")}),-1.0]])]});
            extrude(context, id + "F26", {"entities" : qUnion([Q0, Q1]), "operationType" : NewBodyOperationType.ADD, "depth" : 3.17 * mm});
        }
        {
            var Q0;
            Q0=makeQuery(id+"F24.opExtrude","SWEPT_FACE",FACE,{"disambiguationData":[OSD([sQuery(id+"F23.wireOp",EDGE,"E72.left")])]});
            var sketch = newSketch(context, id + "F27", { "sketchPlane" : qUnion([Q0])});
            skLineSegment(sketch, "E79.bottom", {"start": v(-3.5, 50.16) * mm, "end": v(-15.56, 50.16) * mm, "construction": true});
            skLineSegment(sketch, "E79.top", {"start": v(-3.5, 27.69) * mm, "end": v(-15.56, 27.69) * mm, "construction": true});
            skLineSegment(sketch, "E79.left", {"start": v(-3.5, 50.17) * mm, "end": v(-3.5, 27.69) * mm, "construction": true});
            skLineSegment(sketch, "E79.right", {"start": v(-15.56, 50.16) * mm, "end": v(-15.56, 27.69) * mm, "construction": true});
            skLineSegment(sketch, "E80", {"start": v(-9.53, 57.15) * mm, "end": v(-9.53, 12.7) * mm, "construction": true});
            skPoint(sketch, "E81", {"position": v(-9.53, 27.69) * mm});
            skCircle(sketch, "E82", {"center": v(-9.53, 52.7) * mm, "radius": 1.27 * mm});
            skCircle(sketch, "E83", {"center": v(-9.53, 25.15) * mm, "radius": 1.27 * mm});
            skPoint(sketch, "E84.0", {"position": v(0, 44.45) * mm});
            skLineSegment(sketch, "E85", {"start": v(0, 44.45) * mm, "end": v(-19.05, 44.45) * mm, "construction": true});
            skLineSegment(sketch, "E86.0", {"start": v(-3.24, 50.42) * mm, "end": v(-15.81, 50.42) * mm});
            skLineSegment(sketch, "E86.1", {"start": v(-3.24, 50.42) * mm, "end": v(-3.24, 27.43) * mm});
            skLineSegment(sketch, "E86.2", {"start": v(-3.24, 27.43) * mm, "end": v(-15.81, 27.43) * mm});
            skLineSegment(sketch, "E86.3", {"start": v(-15.81, 50.42) * mm, "end": v(-15.81, 27.43) * mm});
            skSolve(sketch);
        }
        {
            var Q0;
            Q0=makeQuery(id+"F24.opExtrude","SWEPT_FACE",FACE,{"disambiguationData":[OSD([sQuery(id+"F23.wireOp",EDGE,"E71.top")])]});
            var sketch = newSketch(context, id + "F28", { "sketchPlane" : qUnion([Q0])});
            skLineSegment(sketch, "E87.0", {"start": v(-10.67, -3.24) * mm, "end": v(-10.67, -15.81) * mm, "construction": true});
            skLineSegment(sketch, "E88", {"start": v(-10.67, -15.81) * mm, "end": v(-53.6, -15.81) * mm, "construction": true});
            skLineSegment(sketch, "E89", {"start": v(-10.67, -3.24) * mm, "end": v(-57.36, -3.24) * mm, "construction": true});
            skLineSegment(sketch, "E90.bottom", {"start": v(-13.84, -3.24) * mm, "end": v(-36.07, -3.24) * mm});
            skLineSegment(sketch, "E90.top", {"start": v(-13.84, -15.81) * mm, "end": v(-36.07, -15.81) * mm});
            skLineSegment(sketch, "E90.left", {"start": v(-13.84, -3.24) * mm, "end": v(-13.84, -15.81) * mm});
            skLineSegment(sketch, "E90.right", {"start": v(-36.07, -3.24) * mm, "end": v(-36.07, -15.81) * mm});
            skLineSegment(sketch, "E91.0", {"start": v(-10.67, -3.24) * mm, "end": v(-10.67, -15.81) * mm});
            skSolve(sketch);
        }
        {
            var Q0;
            Q0=makeQuery(id+"F28.imprint","IMPRINT",FACE,{"disambiguationData":[TD([[makeQuery(id+"F28.imprint","IMPRINT",EDGE,{"derivedFrom":sQuery(id+"F28.wireOp",EDGE,"E90.bottom")}),1.0]])]});
            extrude(context, id + "F29", {"entities" : qUnion([Q0]), "operationType" : NewBodyOperationType.REMOVE, "oppositeDirection" : true, "depth" : 38.1 * mm});
        }
        {
            var Q0;
            {Q0=qUnion([makeQuery(id+"F27.imprint","IMPRINT",FACE,{"disambiguationData":[TD([[makeQuery(id+"F27.imprint","IMPRINT",EDGE,{"derivedFrom":sQuery(id+"F27.wireOp",EDGE,"E82")}),1.0]])]}),makeQuery(id+"F27.imprint","IMPRINT",FACE,{"disambiguationData":[TD([[makeQuery(id+"F27.imprint","IMPRINT",EDGE,{"derivedFrom":sQuery(id+"F27.wireOp",EDGE,"E83")}),1.0]])]}),makeQuery(id+"F27.imprint","IMPRINT",FACE,{"disambiguationData":[TD([[makeQuery(id+"F27.imprint","IMPRINT",EDGE,{"derivedFrom":sQuery(id+"F27.wireOp",EDGE,"E86.0")}),1.0]])]})]);}
            extrude(context, id + "F30", {"entities" : qUnion([Q0]), "operationType" : NewBodyOperationType.REMOVE, "endBound" : BoundingType.UP_TO_NEXT, "oppositeDirection" : true, "depth" : 25.4 * mm});
        }
        {
            var Q0;
            Q0=makeQuery(id+"F24.opExtrude","SWEPT_FACE",FACE,{"disambiguationData":[OSD([sQuery(id+"F23.wireOp",EDGE,"E72.left")])]});
            var sketch = newSketch(context, id + "F31", { "sketchPlane" : qUnion([Q0])});
            skLineSegment(sketch, "E92.0", {"start": v(-15.81, 50.42) * mm, "end": v(-15.81, 27.43) * mm});
            skLineSegment(sketch, "E93.0", {"start": v(-3.24, 50.42) * mm, "end": v(-15.81, 50.42) * mm});
            skLineSegment(sketch, "E94.0", {"start": v(-3.24, 50.42) * mm, "end": v(-3.24, 27.43) * mm});
            skLineSegment(sketch, "E95.0", {"start": v(-3.24, 27.43) * mm, "end": v(-15.81, 27.43) * mm});
            skCircle(sketch, "E96", {"center": v(-9.53, 44.36) * mm, "radius": 6.04 * mm});
            skCircle(sketch, "E97", {"center": v(-9.53, 44.36) * mm, "radius": 1.59 * mm});
            skSolve(sketch);
        }
        {
            var Q0;
            Q0=makeQuery(id+"F31.imprint","IMPRINT",FACE,{"disambiguationData":[TD([[makeQuery(id+"F31.imprint","IMPRINT",EDGE,{"derivedFrom":sQuery(id+"F31.wireOp",EDGE,"E92.0")}),1.0]])]});
            var Q1;
            Q1=makeQuery(id+"F31.imprint","IMPRINT",FACE,{"disambiguationData":[TD([[makeQuery(id+"F31.imprint","IMPRINT",EDGE,{"derivedFrom":sQuery(id+"F31.wireOp",EDGE,"E96")}),1.0]])]});
            extrude(context, id + "F32", {"entities" : qUnion([Q0, Q1]), "endBound" : BoundingType.SYMMETRIC, "depth" : 12.7 * mm});
        }
        {
            var Q0;
            Q0=makeQuery(id+"F31.imprint","IMPRINT",FACE,{"disambiguationData":[TD([[makeQuery(id+"F31.imprint","IMPRINT",EDGE,{"derivedFrom":sQuery(id+"F31.wireOp",EDGE,"E97")}),1.0]])]});
            extrude(context, id + "F33", {"entities" : qUnion([Q0]), "operationType" : NewBodyOperationType.ADD, "depth" : 25.4 * mm});
        }
    });
